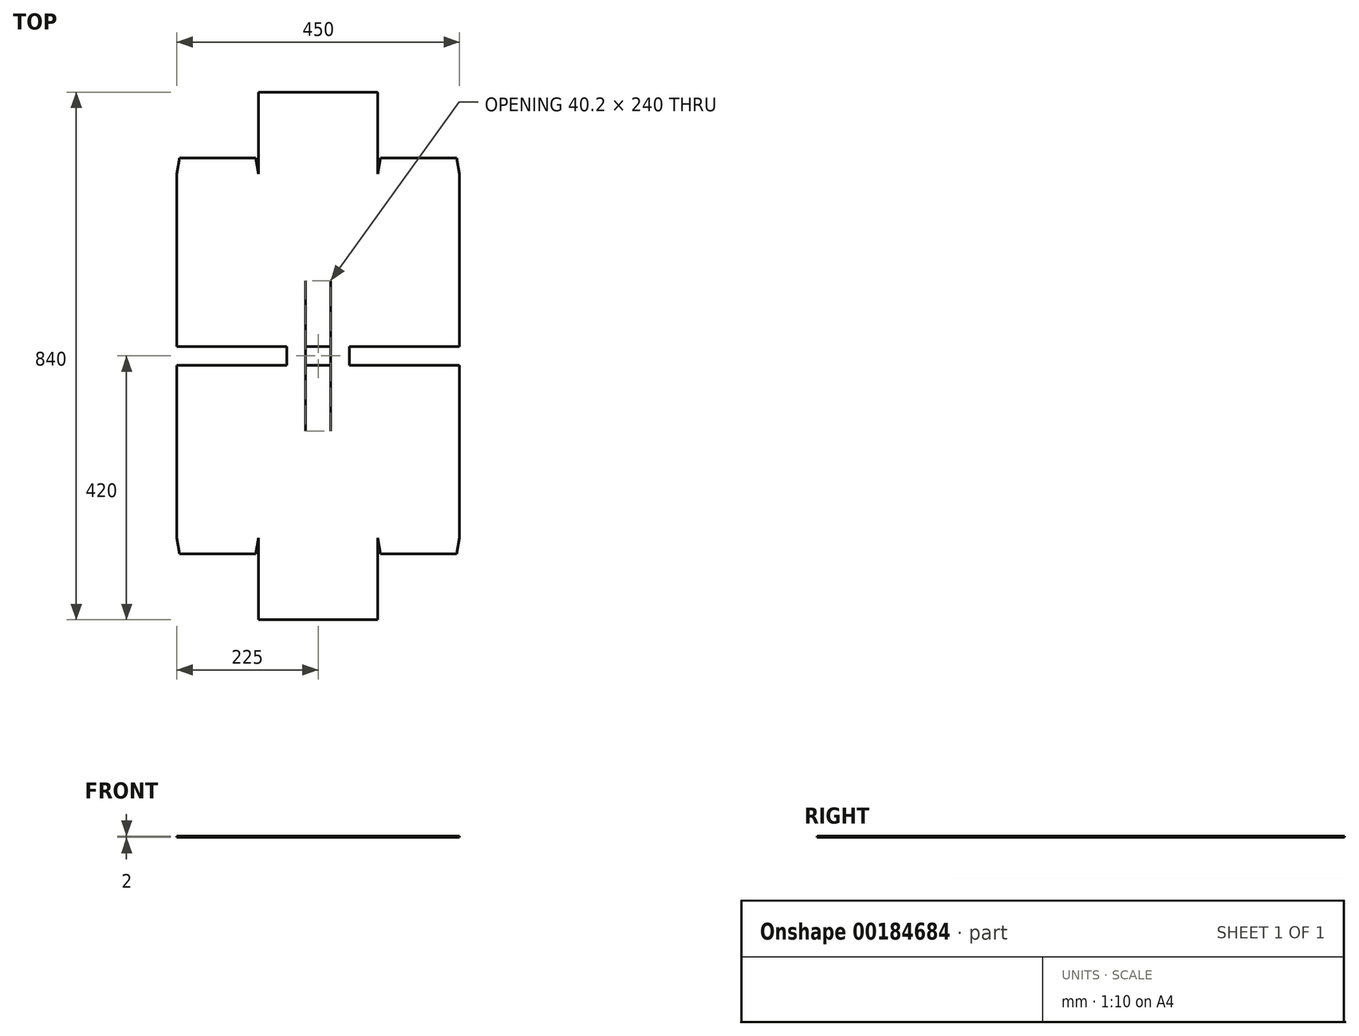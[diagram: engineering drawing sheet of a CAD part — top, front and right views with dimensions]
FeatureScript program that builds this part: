
annotation { "Feature Type Name" : "Feature", "Feature Type Description" : "" }
export const myFeature = defineFeature(function(context is Context, id is Id, definition is map)
    precondition{}
    {
        {
            var Q0;
            Q0=qCreatedBy(makeId("Top.planeOp"),FACE);
            var sketch = newSketch(context, id + "F0", { "sketchPlane" : qUnion([Q0])});
            skLineSegment(sketch, "E0", {"start": v(0, 15) * mm, "end": v(-20, 15) * mm});
            skLineSegment(sketch, "E1", {"start": v(-20, 15) * mm, "end": v(-20, 0) * mm});
            skLineSegment(sketch, "E2", {"start": v(-95, 15) * mm, "end": v(-225, 15) * mm});
            skLineSegment(sketch, "E3", {"start": v(-225, 15) * mm, "end": v(-225, 290) * mm});
            skLineSegment(sketch, "E4", {"start": v(-225, 290) * mm, "end": v(-95, 290) * mm});
            skLineSegment(sketch, "E5", {"start": v(-95, 290) * mm, "end": v(-99.4, 315) * mm});
            skLineSegment(sketch, "E6", {"start": v(-99.4, 315) * mm, "end": v(-220.6, 315) * mm});
            skLineSegment(sketch, "E7", {"start": v(-220.6, 315) * mm, "end": v(-225, 290) * mm});
            skLineSegment(sketch, "E8", {"start": v(-95, 290) * mm, "end": v(-95, 420) * mm});
            skLineSegment(sketch, "E9", {"start": v(-95, 420) * mm, "end": v(0, 420) * mm});
            skLineSegment(sketch, "E10", {"start": v(-50, 15) * mm, "end": v(-50, 0) * mm});
            skLineSegment(sketch, "E11", {"start": v(-19.9, 15) * mm, "end": v(-19.9, 120) * mm});
            skLineSegment(sketch, "E12.MirrorCS", {"start": v(-20.1, 15) * mm, "end": v(-20.1, 120) * mm});
            skLineSegment(sketch, "E13", {"start": v(-20.1, 120) * mm, "end": v(-19.9, 120) * mm});
            skLineSegment(sketch, "E14", {"start": v(-49.9, 15) * mm, "end": v(-49.9, 120) * mm});
            skLineSegment(sketch, "E15.MirrorCS", {"start": v(-50.1, 15) * mm, "end": v(-50.1, 120) * mm});
            skLineSegment(sketch, "E16", {"start": v(-49.9, 15) * mm, "end": v(-50, 15) * mm});
            skLineSegment(sketch, "E17", {"start": v(-20.1, 15) * mm, "end": v(-20, 15) * mm});
            skLineSegment(sketch, "E18", {"start": v(-50.1, 120) * mm, "end": v(-49.9, 120) * mm});
            skLineSegment(sketch, "E19", {"start": v(-50.1, 15) * mm, "end": v(-49.9, 15) * mm});
            skLineSegment(sketch, "E20", {"start": v(-50.1, 15) * mm, "end": v(-95, 15) * mm});
            skLineSegment(sketch, "E21.MirrorCS", {"start": v(-49.9, -15) * mm, "end": v(-50, -15) * mm});
            skLineSegment(sketch, "E22.MirrorCS", {"start": v(-50.1, -15) * mm, "end": v(-49.9, -15) * mm});
            skLineSegment(sketch, "E23.MirrorCS", {"start": v(-20.1, -15) * mm, "end": v(-20, -15) * mm});
            skLineSegment(sketch, "E24.MirrorCS", {"start": v(-50.1, -120) * mm, "end": v(-49.9, -120) * mm});
            skLineSegment(sketch, "E25.MirrorCS", {"start": v(-20.1, -120) * mm, "end": v(-19.9, -120) * mm});
            skLineSegment(sketch, "E26.MirrorCS", {"start": v(-225, -15) * mm, "end": v(-225, -290) * mm});
            skLineSegment(sketch, "E27.MirrorCS", {"start": v(-225, -290) * mm, "end": v(-95, -290) * mm});
            skLineSegment(sketch, "E28.MirrorCS", {"start": v(-95, -290) * mm, "end": v(-99.4, -315) * mm});
            skLineSegment(sketch, "E29.MirrorCS", {"start": v(-50, -15) * mm, "end": v(-50, 0) * mm});
            skLineSegment(sketch, "E30.MirrorCS", {"start": v(-19.9, -15) * mm, "end": v(-19.9, -120) * mm});
            skLineSegment(sketch, "E31.MirrorCS", {"start": v(-95, -290) * mm, "end": v(-95, -420) * mm});
            skLineSegment(sketch, "E32.MirrorCS", {"start": v(-95, -15) * mm, "end": v(-225, -15) * mm});
            skLineSegment(sketch, "E33.MirrorCS", {"start": v(-220.6, -315) * mm, "end": v(-225, -290) * mm});
            skLineSegment(sketch, "E34.MirrorCS", {"start": v(-95, -420) * mm, "end": v(0, -420) * mm});
            skLineSegment(sketch, "E35.MirrorCS", {"start": v(-50.1, -15) * mm, "end": v(-50.1, -120) * mm});
            skLineSegment(sketch, "E36.MirrorCS", {"start": v(-20, -15) * mm, "end": v(-20, 0) * mm});
            skLineSegment(sketch, "E37.MirrorCS", {"start": v(-99.4, -315) * mm, "end": v(-220.6, -315) * mm});
            skLineSegment(sketch, "E38.MirrorCS", {"start": v(-20.1, -15) * mm, "end": v(-20.1, -120) * mm});
            skLineSegment(sketch, "E39.MirrorCS", {"start": v(-49.9, -15) * mm, "end": v(-49.9, -120) * mm});
            skLineSegment(sketch, "E40.MirrorCS", {"start": v(0, -15) * mm, "end": v(-20, -15) * mm});
            skLineSegment(sketch, "E41.MirrorCS", {"start": v(-50.1, -15) * mm, "end": v(-95, -15) * mm});
            skLineSegment(sketch, "E42", {"start": v(0, 420) * mm, "end": v(0, -420) * mm, "construction": true});
            skLineSegment(sketch, "E43.MirrorCS", {"start": v(49.9, -15) * mm, "end": v(50, -15) * mm});
            skLineSegment(sketch, "E44.MirrorCS", {"start": v(50.1, 15) * mm, "end": v(49.9, 15) * mm});
            skLineSegment(sketch, "E45.MirrorCS", {"start": v(50.1, -15) * mm, "end": v(49.9, -15) * mm});
            skLineSegment(sketch, "E46.MirrorCS", {"start": v(49.9, 15) * mm, "end": v(50, 15) * mm});
            skLineSegment(sketch, "E47.MirrorCS", {"start": v(20.1, -15) * mm, "end": v(20, -15) * mm});
            skLineSegment(sketch, "E48.MirrorCS", {"start": v(20.1, 15) * mm, "end": v(20, 15) * mm});
            skLineSegment(sketch, "E49.MirrorCS", {"start": v(220.6, 315) * mm, "end": v(225, 290) * mm});
            skLineSegment(sketch, "E50.MirrorCS", {"start": v(95, 290) * mm, "end": v(99.4, 315) * mm});
            skLineSegment(sketch, "E51.MirrorCS", {"start": v(220.6, -315) * mm, "end": v(225, -290) * mm});
            skLineSegment(sketch, "E52.MirrorCS", {"start": v(95, -290) * mm, "end": v(99.4, -315) * mm});
            skLineSegment(sketch, "E53.MirrorCS", {"start": v(20.1, 120) * mm, "end": v(19.9, 120) * mm});
            skLineSegment(sketch, "E54.MirrorCS", {"start": v(50.1, 120) * mm, "end": v(49.9, 120) * mm});
            skLineSegment(sketch, "E55.MirrorCS", {"start": v(20.1, -120) * mm, "end": v(19.9, -120) * mm});
            skLineSegment(sketch, "E56.MirrorCS", {"start": v(50.1, -120) * mm, "end": v(49.9, -120) * mm});
            skLineSegment(sketch, "E57.MirrorCS", {"start": v(20, 15) * mm, "end": v(20, 0) * mm});
            skLineSegment(sketch, "E58.MirrorCS", {"start": v(50, -15) * mm, "end": v(50, 0) * mm});
            skLineSegment(sketch, "E59.MirrorCS", {"start": v(50, 15) * mm, "end": v(50, 0) * mm});
            skLineSegment(sketch, "E60.MirrorCS", {"start": v(20, -15) * mm, "end": v(20, 0) * mm});
            skLineSegment(sketch, "E61.MirrorCS", {"start": v(19.9, 15) * mm, "end": v(19.9, 120) * mm});
            skLineSegment(sketch, "E62.MirrorCS", {"start": v(50.1, 15) * mm, "end": v(50.1, 120) * mm});
            skLineSegment(sketch, "E63.MirrorCS", {"start": v(0, 15) * mm, "end": v(20, 15) * mm});
            skLineSegment(sketch, "E64.MirrorCS", {"start": v(0, -15) * mm, "end": v(20, -15) * mm});
            skLineSegment(sketch, "E65.MirrorCS", {"start": v(95, -15) * mm, "end": v(225, -15) * mm});
            skLineSegment(sketch, "E66.MirrorCS", {"start": v(20.1, -15) * mm, "end": v(20.1, -120) * mm});
            skLineSegment(sketch, "E67.MirrorCS", {"start": v(95, -420) * mm, "end": v(0, -420) * mm});
            skLineSegment(sketch, "E68.MirrorCS", {"start": v(225, 290) * mm, "end": v(95, 290) * mm});
            skLineSegment(sketch, "E69.MirrorCS", {"start": v(95, -290) * mm, "end": v(95, -420) * mm});
            skLineSegment(sketch, "E70.MirrorCS", {"start": v(99.4, -315) * mm, "end": v(220.6, -315) * mm});
            skLineSegment(sketch, "E71.MirrorCS", {"start": v(225, 15) * mm, "end": v(225, 290) * mm});
            skLineSegment(sketch, "E72.MirrorCS", {"start": v(99.4, 315) * mm, "end": v(220.6, 315) * mm});
            skLineSegment(sketch, "E73.MirrorCS", {"start": v(50.1, -15) * mm, "end": v(50.1, -120) * mm});
            skLineSegment(sketch, "E74.MirrorCS", {"start": v(95, 290) * mm, "end": v(95, 420) * mm});
            skLineSegment(sketch, "E75.MirrorCS", {"start": v(95, 15) * mm, "end": v(225, 15) * mm});
            skLineSegment(sketch, "E76.MirrorCS", {"start": v(95, 420) * mm, "end": v(0, 420) * mm});
            skLineSegment(sketch, "E77.MirrorCS", {"start": v(225, -290) * mm, "end": v(95, -290) * mm});
            skLineSegment(sketch, "E78.MirrorCS", {"start": v(225, -15) * mm, "end": v(225, -290) * mm});
            skLineSegment(sketch, "E79.MirrorCS", {"start": v(20.1, 15) * mm, "end": v(20.1, 120) * mm});
            skLineSegment(sketch, "E80.MirrorCS", {"start": v(49.9, 15) * mm, "end": v(49.9, 120) * mm});
            skLineSegment(sketch, "E81.MirrorCS", {"start": v(50.1, 15) * mm, "end": v(95, 15) * mm});
            skLineSegment(sketch, "E82.MirrorCS", {"start": v(19.9, -15) * mm, "end": v(19.9, -120) * mm});
            skLineSegment(sketch, "E83.MirrorCS", {"start": v(49.9, -15) * mm, "end": v(49.9, -120) * mm});
            skLineSegment(sketch, "E84.MirrorCS", {"start": v(50.1, -15) * mm, "end": v(95, -15) * mm});
            skSolve(sketch);
        }
        {
            var Q0;
            Q0 = qSketchRegion(id + "F0", true);
            extrude(context, id + "F1", {"entities" : qUnion([Q0]), "depth" : 2 * mm});
        }
    });
